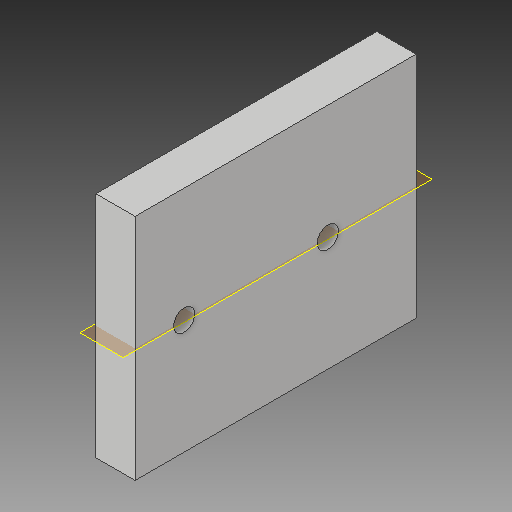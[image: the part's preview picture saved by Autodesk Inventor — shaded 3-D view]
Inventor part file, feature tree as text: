
AUTODESK INVENTOR PART (.ipt)
format: ipt  version: 2018 (Build 220112000, 112)  size: 119,296 bytes
history: native  units: mm
features: reference x5, extrude x4, sketch x4, thread x2, plane x1
ambient origin geometry x8: Origin, YZ Plane, XZ Plane, XY Plane, X Axis, Y Axis, Z Axis, Center Point
bodies: Solid1 (feature_tree)
feature tree (16):
  extrude  "Extrusion1"  Depth=70.0mm
  plane  "Work Plane1"
  extrude  "Extrusion2"  Depth=12.0mm
  extrude  "Extrusion3"  Depth=25.0mm
  extrude  "Extrusion4"  Depth=15.0mm TaperAngle=0.0deg
  thread  "Thread1"  [1 undecoded]
  thread  "Thread2"  [1 undecoded]
  sketch  "Sketch1"  dims[d0=86.0mm d1=70.0mm]
  sketch  "Sketch2"  dims[d2=12.0mm d3=0.0mm d4=6.0mm]
  sketch  "Sketch3"  dims[d5=25.0mm d6=25.0mm]
  reference  "Reference1"
  reference  "Reference2"
  reference  "Reference3"
  sketch  "Sketch4"  dims[d7=15.0mm d8=0.0mm d9=15.0mm d10=0.0mm d11=10.0mm d12=0.0mm d13=0.25mm d14=0.25mm d15=10.0mm d16=0.0mm d17=10.0mm d18=0.0mm]
  reference  "Reference4"
  reference  "Reference5"
note: 2 required parameter values undecoded (feature->parameter linkage not recoverable at this tier; creation-order binding heuristic only, values carry confidence <= 0.55)
